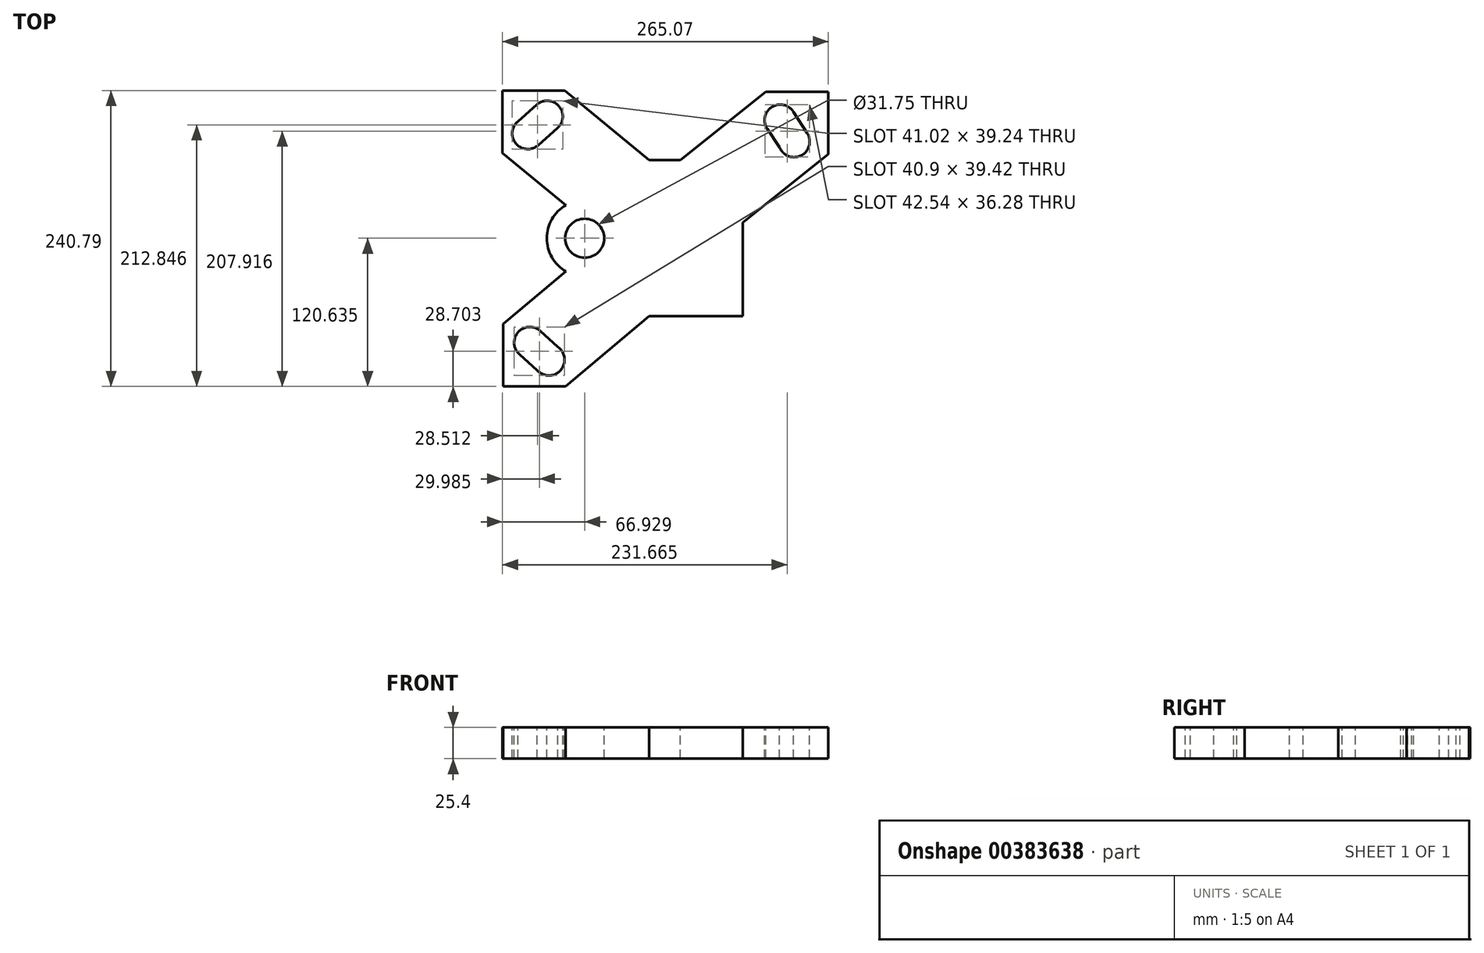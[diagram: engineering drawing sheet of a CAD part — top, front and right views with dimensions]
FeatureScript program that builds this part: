
annotation { "Feature Type Name" : "Feature", "Feature Type Description" : "" }
export const myFeature = defineFeature(function(context is Context, id is Id, definition is map)
    precondition{}
    {
        {
            var Q0;
            Q0=qCreatedBy(makeId("Top.planeOp"),FACE);
            var sketch = newSketch(context, id + "F0", { "sketchPlane" : qUnion([Q0])});
            skLineSegment(sketch, "E0.bottom", {"start": v(-70, 80.79) * mm, "end": v(57, 80.79) * mm});
            skLineSegment(sketch, "E0.top", {"start": v(-70, -46.21) * mm, "end": v(57, -46.21) * mm});
            skLineSegment(sketch, "E0.left", {"start": v(-70, 80.79) * mm, "end": v(-70, -46.21) * mm});
            skLineSegment(sketch, "E0.right", {"start": v(57, 80.79) * mm, "end": v(57, -46.21) * mm});
            skSolve(sketch);
        }
        {
            var Q0;
            Q0 = qSketchRegion(id + "F0", true);
            extrude(context, id + "F1", {"entities" : qUnion([Q0]), "depth" : 25.4 * mm});
        }
        {
            var Q0;
            Q0=makeQuery(id+"F1.opExtrude","CAP_FACE",FACE,{"disambiguationData":[OSD([sQuery(id+"F0.wireOp",EDGE,"E0.bottom"),sQuery(id+"F0.wireOp",EDGE,"E0.top"),sQuery(id+"F0.wireOp",EDGE,"E0.left"),sQuery(id+"F0.wireOp",EDGE,"E0.right")])],"isStart":false});
            var sketch = newSketch(context, id + "F2", { "sketchPlane" : qUnion([Q0])});
            skLineSegment(sketch, "E1", {"start": v(-19.2, 80.79) * mm, "end": v(-87.85, 137.27) * mm});
            skLineSegment(sketch, "E2", {"start": v(-87.85, 137.27) * mm, "end": v(-138.65, 137.27) * mm});
            skLineSegment(sketch, "E3", {"start": v(-138.65, 137.27) * mm, "end": v(-138.65, 86.47) * mm});
            skLineSegment(sketch, "E4", {"start": v(-138.65, 86.47) * mm, "end": v(-70, 29.99) * mm});
            skCircle(sketch, "E5", {"center": v(-118, 102.38) * mm, "radius": 12.7 * mm});
            skCircle(sketch, "E6", {"center": v(-102.3, 116.27) * mm, "radius": 12.7 * mm});
            skLineSegment(sketch, "E7", {"start": v(-126.81, 111.53) * mm, "end": v(-110.72, 125.78) * mm});
            skLineSegment(sketch, "E8", {"start": v(-93.83, 106.8) * mm, "end": v(-109.59, 92.86) * mm});
            skSolve(sketch);
        }
        {
            var Q0;
            {var subQ7=sQuery(id+"F2.wireOp",EDGE,"E1");Q0=makeQuery(id+"F2.imprint","IMPRINT",FACE,{"disambiguationData":[TD([[makeQuery(id+"F2.imprint","IMPRINT",EDGE,{"derivedFrom":subQ7}),1.0]])]});}
            extrude(context, id + "F3", {"entities" : qUnion([Q0]), "operationType" : NewBodyOperationType.ADD, "oppositeDirection" : true, "depth" : 25.4 * mm});
        }
        {
            var Q0;
            {var subQ0=sQuery(id+"F0.wireOp",EDGE,"E0.left");var subQ1=sQuery(id+"F0.wireOp",EDGE,"E0.bottom");Q0=makeQuery(id+"F3.boolean.opBoolean","MERGE",FACE,{"derivedFrom":[makeQuery(id+"F1.opExtrude","CAP_FACE",FACE,{"disambiguationData":[OSD([subQ1,sQuery(id+"F0.wireOp",EDGE,"E0.top"),subQ0,sQuery(id+"F0.wireOp",EDGE,"E0.right")])],"isStart":false}),makeQuery(id+"F3.opExtrude","CAP_FACE",FACE,{"disambiguationData":[OSD([subQ1,subQ0,sQuery(id+"F2.wireOp",EDGE,"E1"),sQuery(id+"F2.wireOp",EDGE,"E2"),sQuery(id+"F2.wireOp",EDGE,"E3"),sQuery(id+"F2.wireOp",EDGE,"E4"),sQuery(id+"F2.wireOp",EDGE,"E5"),sQuery(id+"F2.wireOp",EDGE,"E6"),sQuery(id+"F2.wireOp",EDGE,"E7"),sQuery(id+"F2.wireOp",EDGE,"E8")])],"isStart":true})]});}
            var sketch = newSketch(context, id + "F4", { "sketchPlane" : qUnion([Q0])});
            skLineSegment(sketch, "E9", {"start": v(-70, -46.21) * mm, "end": v(-70, 4.59) * mm});
            skLineSegment(sketch, "E10", {"start": v(-70, 4.59) * mm, "end": v(-137.96, -52.72) * mm});
            skLineSegment(sketch, "E11", {"start": v(-137.96, -52.72) * mm, "end": v(-137.96, -103.52) * mm});
            skLineSegment(sketch, "E12", {"start": v(-137.96, -103.52) * mm, "end": v(-87.16, -103.52) * mm});
            skLineSegment(sketch, "E13", {"start": v(-87.16, -103.52) * mm, "end": v(-19.2, -46.21) * mm});
            skLineSegment(sketch, "E14", {"start": v(-19.2, -46.21) * mm, "end": v(-70, -46.21) * mm});
            skCircle(sketch, "E15", {"center": v(-116.43, -67.79) * mm, "radius": 12.7 * mm});
            skCircle(sketch, "E16", {"center": v(-100.84, -81.83) * mm, "radius": 12.7 * mm});
            skLineSegment(sketch, "E17", {"start": v(-91.25, -73.5) * mm, "end": v(-107.9, -58.39) * mm});
            skLineSegment(sketch, "E18", {"start": v(-110.34, -90.26) * mm, "end": v(-124.9, -77.26) * mm});
            skSolve(sketch);
        }
        {
            var Q0;
            Q0 = qSketchRegion(id + "F4", true);
            extrude(context, id + "F5", {"entities" : qUnion([Q0]), "operationType" : NewBodyOperationType.ADD, "oppositeDirection" : true, "depth" : 25.4 * mm});
        }
        {
            var Q0;
            {var subQ0=sQuery(id+"F0.wireOp",EDGE,"E0.left");var subQ1=sQuery(id+"F0.wireOp",EDGE,"E0.bottom");Q0=makeQuery(id+"F5.boolean.opBoolean","MERGE",FACE,{"derivedFrom":[makeQuery(id+"F3.boolean.opBoolean","MERGE",FACE,{"derivedFrom":[makeQuery(id+"F1.opExtrude","CAP_FACE",FACE,{"disambiguationData":[OSD([subQ1,sQuery(id+"F0.wireOp",EDGE,"E0.top"),subQ0,sQuery(id+"F0.wireOp",EDGE,"E0.right")])],"isStart":false}),makeQuery(id+"F3.opExtrude","CAP_FACE",FACE,{"disambiguationData":[OSD([subQ1,subQ0,sQuery(id+"F2.wireOp",EDGE,"E1"),sQuery(id+"F2.wireOp",EDGE,"E2"),sQuery(id+"F2.wireOp",EDGE,"E3"),sQuery(id+"F2.wireOp",EDGE,"E4"),sQuery(id+"F2.wireOp",EDGE,"E5"),sQuery(id+"F2.wireOp",EDGE,"E6"),sQuery(id+"F2.wireOp",EDGE,"E7"),sQuery(id+"F2.wireOp",EDGE,"E8")])],"isStart":true})]}),makeQuery(id+"F5.opExtrude","CAP_FACE",FACE,{"disambiguationData":[OSD([sQuery(id+"F4.wireOp",EDGE,"E9"),sQuery(id+"F4.wireOp",EDGE,"E10"),sQuery(id+"F4.wireOp",EDGE,"E11"),sQuery(id+"F4.wireOp",EDGE,"E12"),sQuery(id+"F4.wireOp",EDGE,"E13"),sQuery(id+"F4.wireOp",EDGE,"E14"),sQuery(id+"F4.wireOp",EDGE,"E15"),sQuery(id+"F4.wireOp",EDGE,"E16"),sQuery(id+"F4.wireOp",EDGE,"E17"),sQuery(id+"F4.wireOp",EDGE,"E18")])],"isStart":true})]});}
            var sketch = newSketch(context, id + "F6", { "sketchPlane" : qUnion([Q0])});
            skLineSegment(sketch, "E19", {"start": v(-70, 4.59) * mm, "end": v(-103.98, -24.07) * mm});
            skLineSegment(sketch, "E20", {"start": v(-103.98, -24.07) * mm, "end": v(-103.98, 57.95) * mm});
            skLineSegment(sketch, "E21", {"start": v(-103.98, 57.95) * mm, "end": v(-70, 29.99) * mm});
            skLineSegment(sketch, "E22", {"start": v(-70, 29.99) * mm, "end": v(-70, 4.59) * mm});
            skArc(sketch, "E23", {"start": v(-87, 43.97) * mm, "mid": v(-102.61, 17.12) * mm, "end": v(-87, -9.74) * mm});
            skSolve(sketch);
        }
        {
            var Q0;
            {var subQ0=sQuery(id+"F6.wireOp",EDGE,"E22");Q0=makeQuery(id+"F6.imprint","IMPRINT",FACE,{"disambiguationData":[TD([[makeQuery(id+"F6.imprint","IMPRINT",EDGE,{"derivedFrom":subQ0}),-1.0]])]});}
            extrude(context, id + "F7", {"entities" : qUnion([Q0]), "operationType" : NewBodyOperationType.ADD, "oppositeDirection" : true, "depth" : 25.4 * mm});
        }
        {
            var Q0;
            {var subQ0=sQuery(id+"F0.wireOp",EDGE,"E0.left");var subQ1=sQuery(id+"F0.wireOp",EDGE,"E0.bottom");Q0=makeQuery(id+"F7.boolean.opBoolean","MERGE",FACE,{"derivedFrom":[makeQuery(id+"F5.boolean.opBoolean","MERGE",FACE,{"derivedFrom":[makeQuery(id+"F3.boolean.opBoolean","MERGE",FACE,{"derivedFrom":[makeQuery(id+"F1.opExtrude","CAP_FACE",FACE,{"disambiguationData":[OSD([subQ1,sQuery(id+"F0.wireOp",EDGE,"E0.top"),subQ0,sQuery(id+"F0.wireOp",EDGE,"E0.right")])],"isStart":false}),makeQuery(id+"F3.opExtrude","CAP_FACE",FACE,{"disambiguationData":[OSD([subQ1,subQ0,sQuery(id+"F2.wireOp",EDGE,"E1"),sQuery(id+"F2.wireOp",EDGE,"E2"),sQuery(id+"F2.wireOp",EDGE,"E3"),sQuery(id+"F2.wireOp",EDGE,"E4"),sQuery(id+"F2.wireOp",EDGE,"E5"),sQuery(id+"F2.wireOp",EDGE,"E6"),sQuery(id+"F2.wireOp",EDGE,"E7"),sQuery(id+"F2.wireOp",EDGE,"E8")])],"isStart":true})]}),makeQuery(id+"F5.opExtrude","CAP_FACE",FACE,{"disambiguationData":[OSD([sQuery(id+"F4.wireOp",EDGE,"E9"),sQuery(id+"F4.wireOp",EDGE,"E10"),sQuery(id+"F4.wireOp",EDGE,"E11"),sQuery(id+"F4.wireOp",EDGE,"E12"),sQuery(id+"F4.wireOp",EDGE,"E13"),sQuery(id+"F4.wireOp",EDGE,"E14"),sQuery(id+"F4.wireOp",EDGE,"E15"),sQuery(id+"F4.wireOp",EDGE,"E16"),sQuery(id+"F4.wireOp",EDGE,"E17"),sQuery(id+"F4.wireOp",EDGE,"E18")])],"isStart":true})]}),makeQuery(id+"F7.opExtrude","CAP_FACE",FACE,{"disambiguationData":[OSD([sQuery(id+"F6.wireOp",EDGE,"E19"),sQuery(id+"F6.wireOp",EDGE,"E21"),sQuery(id+"F6.wireOp",EDGE,"E22"),sQuery(id+"F6.wireOp",EDGE,"E23")])],"isStart":true})]});}
            var sketch = newSketch(context, id + "F8", { "sketchPlane" : qUnion([Q0])});
            skCircle(sketch, "E24", {"center": v(-71.72, 17.12) * mm, "radius": 15.88 * mm});
            skSolve(sketch);
        }
        {
            var Q0;
            Q0 = qSketchRegion(id + "F8", true);
            extrude(context, id + "F9", {"entities" : qUnion([Q0]), "operationType" : NewBodyOperationType.REMOVE, "oppositeDirection" : true, "depth" : 25.4 * mm});
        }
        {
            var Q0;
            {var subQ0=sQuery(id+"F0.wireOp",EDGE,"E0.left");var subQ1=sQuery(id+"F0.wireOp",EDGE,"E0.bottom");Q0=makeQuery(id+"F7.boolean.opBoolean","MERGE",FACE,{"derivedFrom":[makeQuery(id+"F5.boolean.opBoolean","MERGE",FACE,{"derivedFrom":[makeQuery(id+"F3.boolean.opBoolean","MERGE",FACE,{"derivedFrom":[makeQuery(id+"F1.opExtrude","CAP_FACE",FACE,{"disambiguationData":[OSD([subQ1,sQuery(id+"F0.wireOp",EDGE,"E0.top"),subQ0,sQuery(id+"F0.wireOp",EDGE,"E0.right")])],"isStart":false}),makeQuery(id+"F3.opExtrude","CAP_FACE",FACE,{"disambiguationData":[OSD([subQ1,subQ0,sQuery(id+"F2.wireOp",EDGE,"E1"),sQuery(id+"F2.wireOp",EDGE,"E2"),sQuery(id+"F2.wireOp",EDGE,"E3"),sQuery(id+"F2.wireOp",EDGE,"E4"),sQuery(id+"F2.wireOp",EDGE,"E5"),sQuery(id+"F2.wireOp",EDGE,"E6"),sQuery(id+"F2.wireOp",EDGE,"E7"),sQuery(id+"F2.wireOp",EDGE,"E8")])],"isStart":true})]}),makeQuery(id+"F5.opExtrude","CAP_FACE",FACE,{"disambiguationData":[OSD([sQuery(id+"F4.wireOp",EDGE,"E9"),sQuery(id+"F4.wireOp",EDGE,"E10"),sQuery(id+"F4.wireOp",EDGE,"E11"),sQuery(id+"F4.wireOp",EDGE,"E12"),sQuery(id+"F4.wireOp",EDGE,"E13"),sQuery(id+"F4.wireOp",EDGE,"E14"),sQuery(id+"F4.wireOp",EDGE,"E15"),sQuery(id+"F4.wireOp",EDGE,"E16"),sQuery(id+"F4.wireOp",EDGE,"E17"),sQuery(id+"F4.wireOp",EDGE,"E18")])],"isStart":true})]}),makeQuery(id+"F7.opExtrude","CAP_FACE",FACE,{"disambiguationData":[OSD([sQuery(id+"F6.wireOp",EDGE,"E19"),sQuery(id+"F6.wireOp",EDGE,"E21"),sQuery(id+"F6.wireOp",EDGE,"E22"),sQuery(id+"F6.wireOp",EDGE,"E23")])],"isStart":true})]});}
            var sketch = newSketch(context, id + "F10", { "sketchPlane" : qUnion([Q0])});
            skLineSegment(sketch, "E25", {"start": v(57, 80.79) * mm, "end": v(6.2, 80.79) * mm});
            skLineSegment(sketch, "E26", {"start": v(6.2, 80.79) * mm, "end": v(75.62, 136.32) * mm});
            skLineSegment(sketch, "E27", {"start": v(75.62, 136.32) * mm, "end": v(126.42, 136.32) * mm});
            skLineSegment(sketch, "E28", {"start": v(126.42, 136.32) * mm, "end": v(126.42, 85.52) * mm});
            skLineSegment(sketch, "E29", {"start": v(126.42, 85.52) * mm, "end": v(57, 29.99) * mm});
            skLineSegment(sketch, "E30", {"start": v(57, 29.99) * mm, "end": v(57, 80.79) * mm});
            skCircle(sketch, "E31", {"center": v(87.34, 113.17) * mm, "radius": 12.7 * mm});
            skCircle(sketch, "E32", {"center": v(98.62, 95.8) * mm, "radius": 12.7 * mm});
            skLineSegment(sketch, "E33", {"start": v(98.1, 119.91) * mm, "end": v(109.26, 102.73) * mm});
            skLineSegment(sketch, "E34", {"start": v(76.6, 106.4) * mm, "end": v(87.34, 89.85) * mm});
            skSolve(sketch);
        }
        {
            var Q0;
            Q0 = qSketchRegion(id + "F10", true);
            extrude(context, id + "F11", {"entities" : qUnion([Q0]), "operationType" : NewBodyOperationType.ADD, "oppositeDirection" : true, "depth" : 25.4 * mm});
        }
        {
            var Q0;
            {var subQ0=sQuery(id+"F0.wireOp",EDGE,"E0.left");var subQ1=sQuery(id+"F0.wireOp",EDGE,"E0.bottom");Q0=makeQuery(id+"F11.boolean.opBoolean","MERGE",FACE,{"derivedFrom":[makeQuery(id+"F7.boolean.opBoolean","MERGE",FACE,{"derivedFrom":[makeQuery(id+"F5.boolean.opBoolean","MERGE",FACE,{"derivedFrom":[makeQuery(id+"F3.boolean.opBoolean","MERGE",FACE,{"derivedFrom":[makeQuery(id+"F1.opExtrude","CAP_FACE",FACE,{"disambiguationData":[OSD([subQ1,sQuery(id+"F0.wireOp",EDGE,"E0.top"),subQ0,sQuery(id+"F0.wireOp",EDGE,"E0.right")])],"isStart":false}),makeQuery(id+"F3.opExtrude","CAP_FACE",FACE,{"disambiguationData":[OSD([subQ1,subQ0,sQuery(id+"F2.wireOp",EDGE,"E1"),sQuery(id+"F2.wireOp",EDGE,"E2"),sQuery(id+"F2.wireOp",EDGE,"E3"),sQuery(id+"F2.wireOp",EDGE,"E4"),sQuery(id+"F2.wireOp",EDGE,"E5"),sQuery(id+"F2.wireOp",EDGE,"E6"),sQuery(id+"F2.wireOp",EDGE,"E7"),sQuery(id+"F2.wireOp",EDGE,"E8")])],"isStart":true})]}),makeQuery(id+"F5.opExtrude","CAP_FACE",FACE,{"disambiguationData":[OSD([sQuery(id+"F4.wireOp",EDGE,"E9"),sQuery(id+"F4.wireOp",EDGE,"E10"),sQuery(id+"F4.wireOp",EDGE,"E11"),sQuery(id+"F4.wireOp",EDGE,"E12"),sQuery(id+"F4.wireOp",EDGE,"E13"),sQuery(id+"F4.wireOp",EDGE,"E14"),sQuery(id+"F4.wireOp",EDGE,"E15"),sQuery(id+"F4.wireOp",EDGE,"E16"),sQuery(id+"F4.wireOp",EDGE,"E17"),sQuery(id+"F4.wireOp",EDGE,"E18")])],"isStart":true})]}),makeQuery(id+"F7.opExtrude","CAP_FACE",FACE,{"disambiguationData":[OSD([sQuery(id+"F6.wireOp",EDGE,"E19"),sQuery(id+"F6.wireOp",EDGE,"E21"),sQuery(id+"F6.wireOp",EDGE,"E22"),sQuery(id+"F6.wireOp",EDGE,"E23")])],"isStart":true})]}),makeQuery(id+"F11.opExtrude","CAP_FACE",FACE,{"disambiguationData":[OSD([sQuery(id+"F10.wireOp",EDGE,"E25"),sQuery(id+"F10.wireOp",EDGE,"E26"),sQuery(id+"F10.wireOp",EDGE,"E27"),sQuery(id+"F10.wireOp",EDGE,"E28"),sQuery(id+"F10.wireOp",EDGE,"E29"),sQuery(id+"F10.wireOp",EDGE,"E30"),sQuery(id+"F10.wireOp",EDGE,"E31"),sQuery(id+"F10.wireOp",EDGE,"E32"),sQuery(id+"F10.wireOp",EDGE,"E33")])],"isStart":true})]});}
            var sketch = newSketch(context, id + "F12", { "sketchPlane" : qUnion([Q0])});
            skLineSegment(sketch, "E35", {"start": v(6.2, 80.79) * mm, "end": v(-19.2, 80.79) * mm});
            skLineSegment(sketch, "E36", {"start": v(-19.2, 80.79) * mm, "end": v(-53.52, 109.03) * mm});
            skLineSegment(sketch, "E37", {"start": v(-53.52, 109.03) * mm, "end": v(41.5, 109.03) * mm});
            skLineSegment(sketch, "E38", {"start": v(41.5, 109.03) * mm, "end": v(6.2, 80.79) * mm});
            skArc(sketch, "E39", {"start": v(23.85, 94.9) * mm, "mid": v(-6.25, 107.63) * mm, "end": v(-36.36, 94.9) * mm});
            skSolve(sketch);
        }
        {
            var Q0;
            {var subQ0=sQuery(id+"F12.wireOp",EDGE,"E35");Q0=makeQuery(id+"F12.imprint","IMPRINT",FACE,{"disambiguationData":[TD([[makeQuery(id+"F12.imprint","IMPRINT",EDGE,{"derivedFrom":subQ0}),1.0]])]});}
            extrude(context, id + "F13", {"entities" : qUnion([Q0]), "operationType" : NewBodyOperationType.REMOVE, "oppositeDirection" : true, "depth" : 25.4 * mm});
        }
        {
            var Q0;
            {var subQ0=sQuery(id+"F0.wireOp",EDGE,"E0.left");var subQ1=sQuery(id+"F0.wireOp",EDGE,"E0.bottom");Q0=makeQuery(id+"F11.boolean.opBoolean","MERGE",FACE,{"derivedFrom":[makeQuery(id+"F7.boolean.opBoolean","MERGE",FACE,{"derivedFrom":[makeQuery(id+"F5.boolean.opBoolean","MERGE",FACE,{"derivedFrom":[makeQuery(id+"F3.boolean.opBoolean","MERGE",FACE,{"derivedFrom":[makeQuery(id+"F1.opExtrude","CAP_FACE",FACE,{"disambiguationData":[OSD([subQ1,sQuery(id+"F0.wireOp",EDGE,"E0.top"),subQ0,sQuery(id+"F0.wireOp",EDGE,"E0.right")])],"isStart":false}),makeQuery(id+"F3.opExtrude","CAP_FACE",FACE,{"disambiguationData":[OSD([subQ1,subQ0,sQuery(id+"F2.wireOp",EDGE,"E1"),sQuery(id+"F2.wireOp",EDGE,"E2"),sQuery(id+"F2.wireOp",EDGE,"E3"),sQuery(id+"F2.wireOp",EDGE,"E4"),sQuery(id+"F2.wireOp",EDGE,"E5"),sQuery(id+"F2.wireOp",EDGE,"E6"),sQuery(id+"F2.wireOp",EDGE,"E7"),sQuery(id+"F2.wireOp",EDGE,"E8")])],"isStart":true})]}),makeQuery(id+"F5.opExtrude","CAP_FACE",FACE,{"disambiguationData":[OSD([sQuery(id+"F4.wireOp",EDGE,"E9"),sQuery(id+"F4.wireOp",EDGE,"E10"),sQuery(id+"F4.wireOp",EDGE,"E11"),sQuery(id+"F4.wireOp",EDGE,"E12"),sQuery(id+"F4.wireOp",EDGE,"E13"),sQuery(id+"F4.wireOp",EDGE,"E14"),sQuery(id+"F4.wireOp",EDGE,"E15"),sQuery(id+"F4.wireOp",EDGE,"E16"),sQuery(id+"F4.wireOp",EDGE,"E17"),sQuery(id+"F4.wireOp",EDGE,"E18")])],"isStart":true})]}),makeQuery(id+"F7.opExtrude","CAP_FACE",FACE,{"disambiguationData":[OSD([sQuery(id+"F6.wireOp",EDGE,"E19"),sQuery(id+"F6.wireOp",EDGE,"E21"),sQuery(id+"F6.wireOp",EDGE,"E22"),sQuery(id+"F6.wireOp",EDGE,"E23")])],"isStart":true})]}),makeQuery(id+"F11.opExtrude","CAP_FACE",FACE,{"disambiguationData":[OSD([sQuery(id+"F10.wireOp",EDGE,"E25"),sQuery(id+"F10.wireOp",EDGE,"E26"),sQuery(id+"F10.wireOp",EDGE,"E27"),sQuery(id+"F10.wireOp",EDGE,"E28"),sQuery(id+"F10.wireOp",EDGE,"E29"),sQuery(id+"F10.wireOp",EDGE,"E30"),sQuery(id+"F10.wireOp",EDGE,"E31"),sQuery(id+"F10.wireOp",EDGE,"E32"),sQuery(id+"F10.wireOp",EDGE,"E33")])],"isStart":true})]});}
            var sketch = newSketch(context, id + "F14", { "sketchPlane" : qUnion([Q0])});
            skLineSegment(sketch, "E40", {"start": v(86.8, 91.13) * mm, "end": v(76.78, 106.1) * mm});
            skSolve(sketch);
        }
        {
            var Q0;
            Q0 = qSketchRegion(id + "F14", true);
            var Q1;
            {var subQ0=sQuery(id+"F14.wireOp",EDGE,"E40");Q1=makeQuery(id+"F14.imprint","IMPRINT",FACE,{"disambiguationData":[TD([[makeQuery(id+"F14.imprint","IMPRINT",EDGE,{"derivedFrom":subQ0}),-1.0]])]});}
            extrude(context, id + "F15", {"entities" : qUnion([Q0, Q1]), "operationType" : NewBodyOperationType.REMOVE, "oppositeDirection" : true, "depth" : 25.4 * mm});
        }
    });
